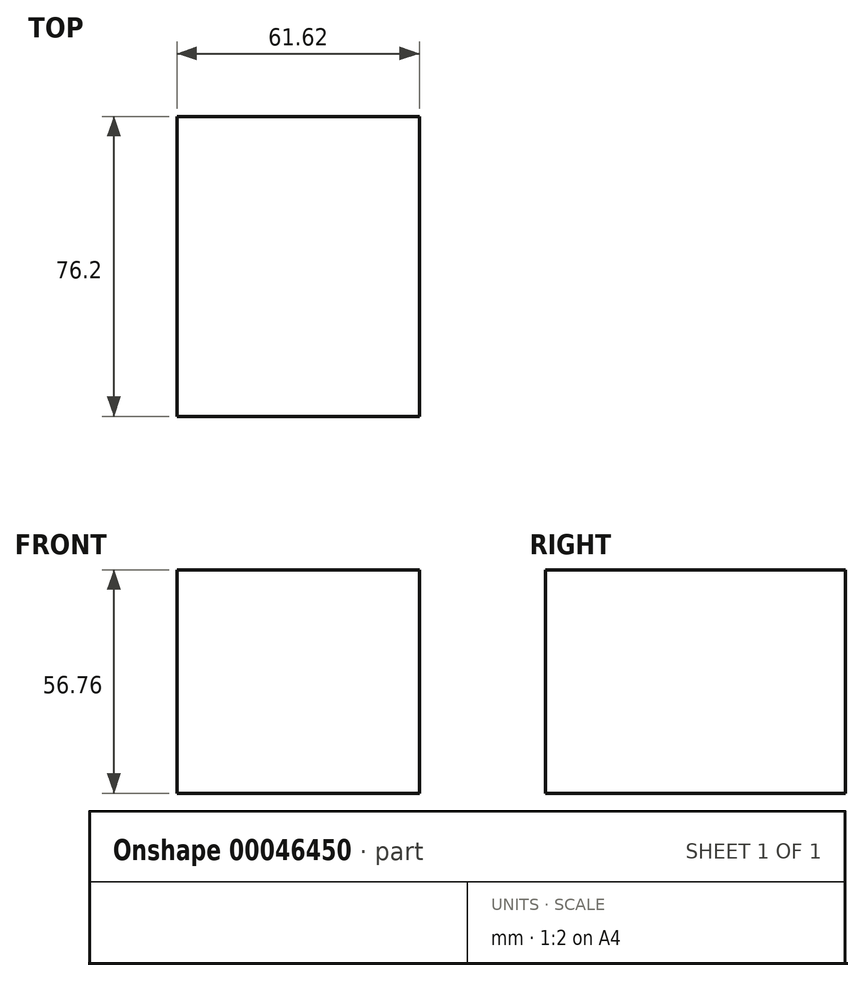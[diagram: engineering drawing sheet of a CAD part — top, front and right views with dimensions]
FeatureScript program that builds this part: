
annotation { "Feature Type Name" : "Feature", "Feature Type Description" : "" }
export const myFeature = defineFeature(function(context is Context, id is Id, definition is map)
    precondition{}
    {
        {
            var Q0;
            Q0=qCreatedBy(makeId("Front.planeOp"),FACE);
            var sketch = newSketch(context, id + "F0", { "sketchPlane" : qUnion([Q0])});
            skLineSegment(sketch, "E0.rect.bottom", {"start": v(30.8, 28.38) * mm, "end": v(-30.8, 28.38) * mm});
            skLineSegment(sketch, "E0.rect.top", {"start": v(30.8, -28.38) * mm, "end": v(-30.8, -28.38) * mm});
            skLineSegment(sketch, "E0.rect.left", {"start": v(30.8, 28.38) * mm, "end": v(30.8, -28.38) * mm});
            skLineSegment(sketch, "E0.rect.right", {"start": v(-30.8, 28.38) * mm, "end": v(-30.8, -28.38) * mm});
            skPoint(sketch, "E0.rect.middle", {"position": v(0, 0) * mm});
            skSolve(sketch);
        }
        {
            var Q0;
            Q0 = qSketchRegion(id + "F0", true);
            extrude(context, id + "F1", {"entities" : qUnion([Q0]), "endBound" : BoundingType.SYMMETRIC, "depth" : 76.2 * mm});
        }
    });
